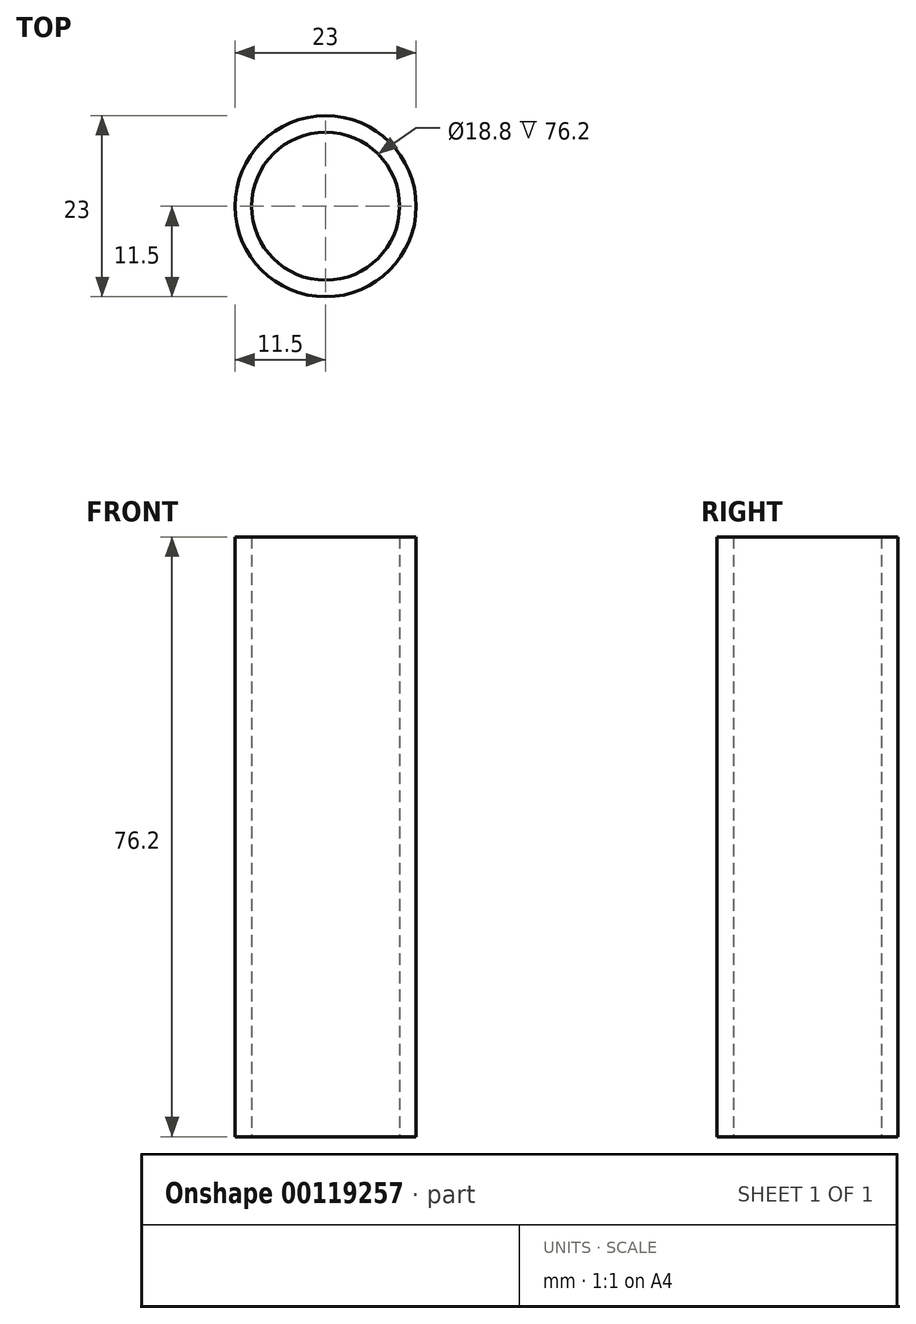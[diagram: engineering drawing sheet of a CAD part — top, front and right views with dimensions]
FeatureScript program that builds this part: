
annotation { "Feature Type Name" : "Feature", "Feature Type Description" : "" }
export const myFeature = defineFeature(function(context is Context, id is Id, definition is map)
    precondition{}
    {
        {
            var Q0;
            Q0=qCreatedBy(makeId("Top.planeOp"),FACE);
            var sketch = newSketch(context, id + "F0", { "sketchPlane" : qUnion([Q0])});
            skCircle(sketch, "E0", {"center": v(0, 0) * mm, "radius": 11.5 * mm});
            skCircle(sketch, "E1", {"center": v(0, 0) * mm, "radius": 9.4 * mm});
            skSolve(sketch);
        }
        {
            var Q0;
            Q0=makeQuery(id+"F0.imprint","IMPRINT",FACE,{"disambiguationData":[TD([[makeQuery(id+"F0.imprint","IMPRINT",EDGE,{"derivedFrom":sQuery(id+"F0.wireOp",EDGE,"E0")}),1.0]])]});
            extrude(context, id + "F1", {"entities" : qUnion([Q0]), "depth" : 76.2 * mm});
        }
    });
